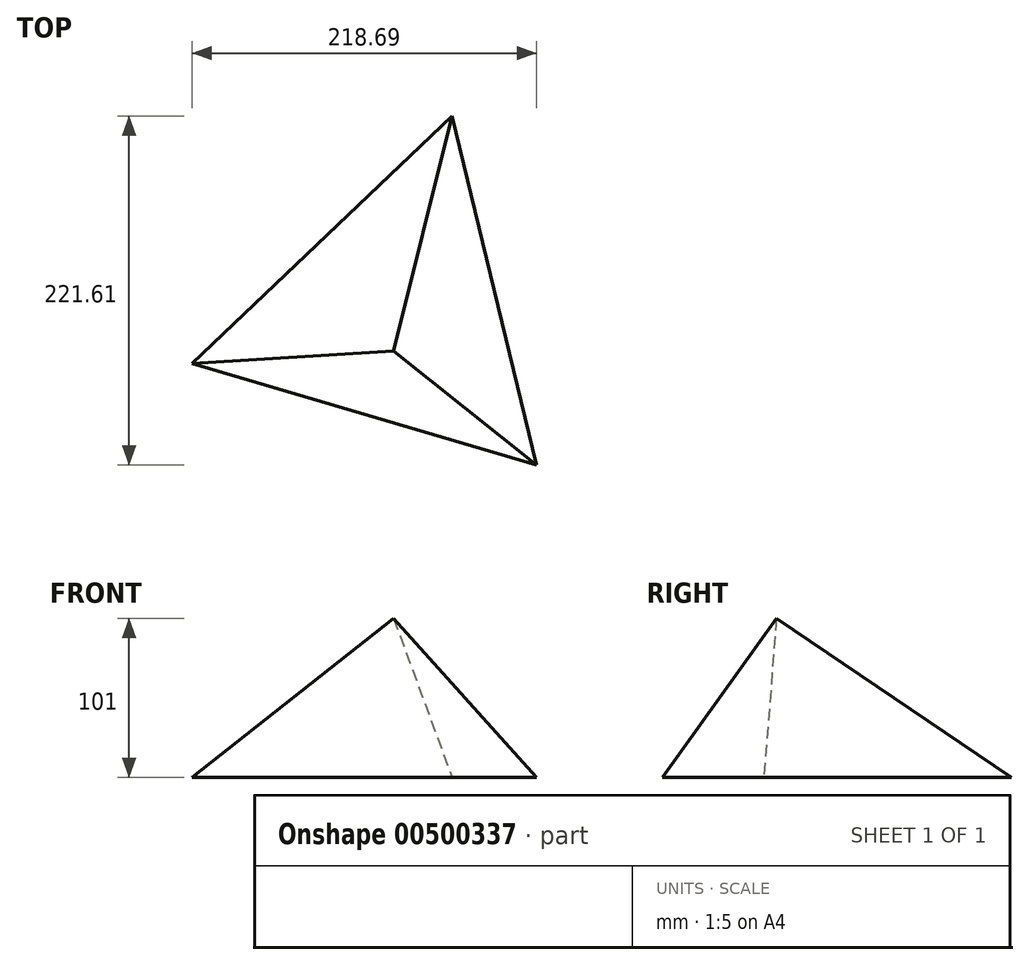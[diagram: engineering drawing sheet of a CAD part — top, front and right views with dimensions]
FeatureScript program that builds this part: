
annotation { "Feature Type Name" : "Feature", "Feature Type Description" : "" }
export const myFeature = defineFeature(function(context is Context, id is Id, definition is map)
    precondition{}
    {
        {
            var Q0;
            Q0=qCreatedBy(makeId("Top.planeOp"),FACE);
            var sketch = newSketch(context, id + "F0", { "sketchPlane" : qUnion([Q0])});
            skCircle(sketch, "E0.cCircle", {"center": v(0, 0) * mm, "radius": 131.63 * mm, "construction": true});
            skLineSegment(sketch, "E0.0", {"start": v(-127.95, -30.9) * mm, "end": v(37.2, 126.26) * mm});
            skLineSegment(sketch, "E0.1", {"start": v(37.2, 126.26) * mm, "end": v(90.74, -95.35) * mm});
            skLineSegment(sketch, "E0.2", {"start": v(90.74, -95.35) * mm, "end": v(-127.95, -30.9) * mm});
            skSolve(sketch);
        }
        {
            var Q0;
            Q0=qCreatedBy(makeId("Top.planeOp"),FACE);
            cPlane(context, id + "F1", {"entities" : qUnion([Q0]), "cplaneType" : CPlaneType.OFFSET, "offset" : 101 * mm, "width" : 150 * mm, "height" : 150 * mm});
        }
        {
            var Q0;
            Q0=qCreatedBy(id+"F1.planeOp",FACE);
            var sketch = newSketch(context, id + "F2", { "sketchPlane" : qUnion([Q0])});
            skPoint(sketch, "E1", {"position": v(0, -22.9) * mm});
            skSolve(sketch);
        }
        {
            var Q0;
            Q0=sQuery(id+"F2.wireOp",VERTEX,"E1");
            var Q1;
            Q1=makeQuery(id+"F0.imprint","IMPRINT",FACE,{"disambiguationData":[TD([[makeQuery(id+"F0.imprint","IMPRINT",EDGE,{"derivedFrom":sQuery(id+"F0.wireOp",EDGE,"E0.0")}),-1.0]])]});
            loft(context, id + "F3", {"sheetProfilesArray" : [{ "sheetProfileEntities" : qUnion([Q0]) }, { "sheetProfileEntities" : qUnion([Q1]) }]});
        }
    });
